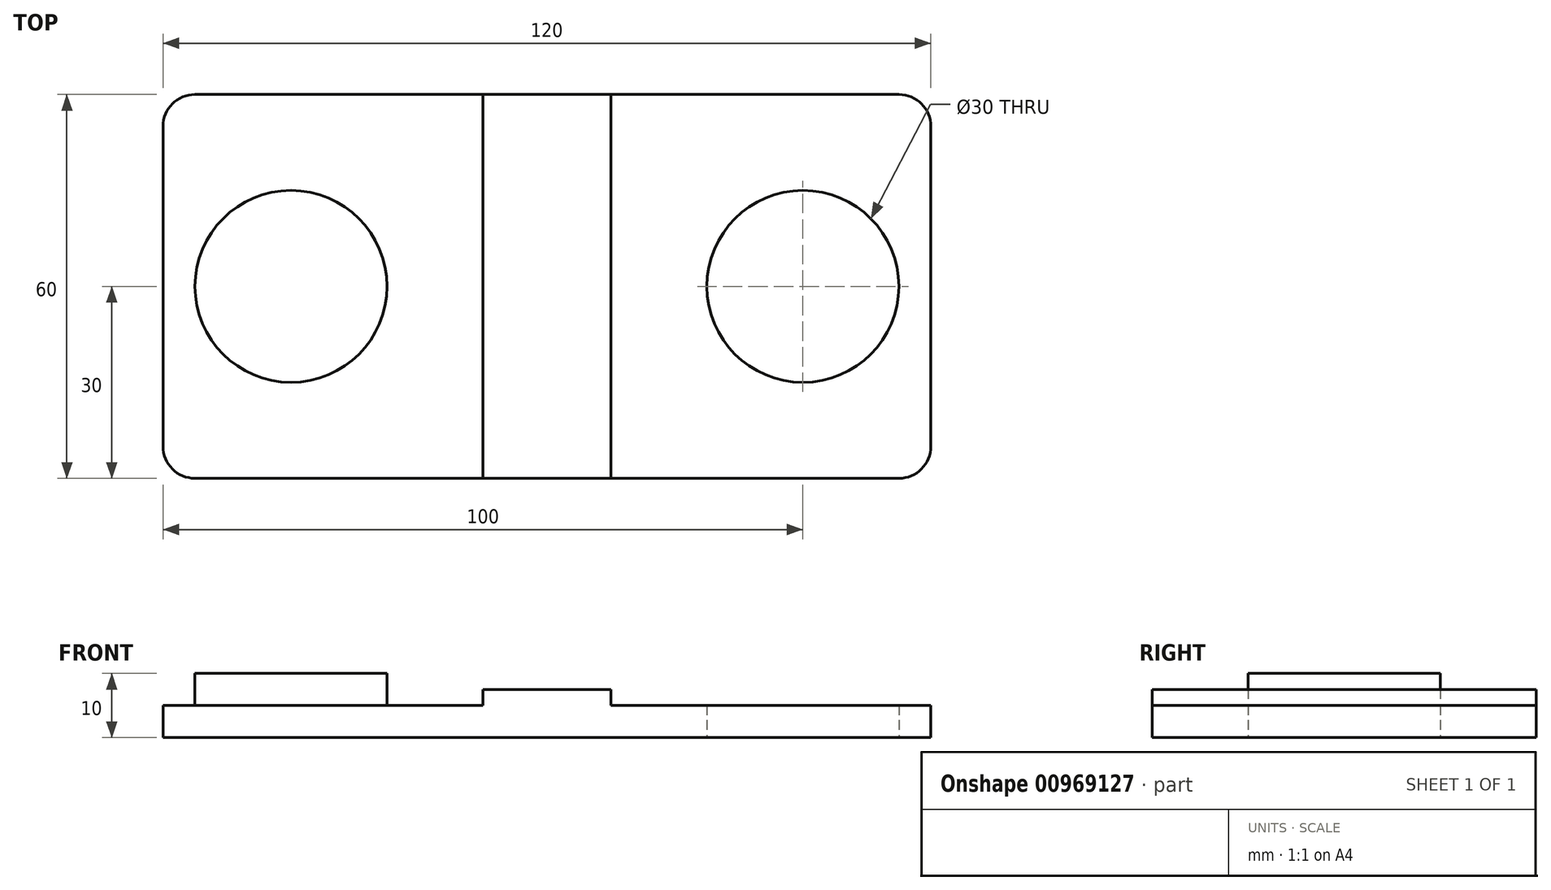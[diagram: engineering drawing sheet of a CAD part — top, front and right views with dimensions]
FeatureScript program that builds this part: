
annotation { "Feature Type Name" : "Feature", "Feature Type Description" : "" }
export const myFeature = defineFeature(function(context is Context, id is Id, definition is map)
    precondition{}
    {
        {
            var Q0;
            Q0=qCreatedBy(makeId("Top.planeOp"),FACE);
            var sketch = newSketch(context, id + "F0", { "sketchPlane" : qUnion([Q0])});
            skLineSegment(sketch, "E0.bottom", {"start": v(60, 30) * mm, "end": v(-60, 30) * mm});
            skLineSegment(sketch, "E0.top", {"start": v(60, -30) * mm, "end": v(-60, -30) * mm});
            skLineSegment(sketch, "E0.left", {"start": v(60, 30) * mm, "end": v(60, -30) * mm});
            skLineSegment(sketch, "E0.right", {"start": v(-60, 30) * mm, "end": v(-60, -30) * mm});
            skPoint(sketch, "E0.middle", {"position": v(0, 0) * mm});
            skCircle(sketch, "E1", {"center": v(40, 0) * mm, "radius": 15 * mm});
            skSolve(sketch);
        }
        {
            var Q0;
            Q0=makeQuery(id+"F0.imprint","IMPRINT",FACE,{"disambiguationData":[TD([[makeQuery(id+"F0.imprint","IMPRINT",EDGE,{"derivedFrom":sQuery(id+"F0.wireOp",EDGE,"E0.bottom")}),1.0]])]});
            extrude(context, id + "F1", {"entities" : qUnion([Q0]), "depth" : 5 * mm, "offsetDistance" : 25 * mm});
        }
        {
            var Q0;
            Q0=makeQuery(id+"F1.opExtrude","SWEPT_EDGE",EDGE,{"disambiguationData":[OSD([sQuery(id+"F0.wireOp",EDGE,"E0.bottom"),sQuery(id+"F0.wireOp",EDGE,"E0.left")])]});
            var Q1;
            Q1=makeQuery(id+"F1.opExtrude","SWEPT_EDGE",EDGE,{"disambiguationData":[OSD([sQuery(id+"F0.wireOp",EDGE,"E0.top"),sQuery(id+"F0.wireOp",EDGE,"E0.left")])]});
            var Q2;
            Q2=makeQuery(id+"F1.opExtrude","SWEPT_EDGE",EDGE,{"disambiguationData":[OSD([sQuery(id+"F0.wireOp",EDGE,"E0.top"),sQuery(id+"F0.wireOp",EDGE,"E0.right")])]});
            var Q3;
            Q3=makeQuery(id+"F1.opExtrude","SWEPT_EDGE",EDGE,{"disambiguationData":[OSD([sQuery(id+"F0.wireOp",EDGE,"E0.bottom"),sQuery(id+"F0.wireOp",EDGE,"E0.right")])]});
            fillet(context, id + "F2", {"entities" : qUnion([Q0, Q1, Q2, Q3]), "radius" : 5 * mm, "tangentPropagation" : true, "allowEdgeOverflow" : false});
        }
        {
            var Q0;
            Q0=makeQuery(id+"F1.opExtrude","CAP_FACE",FACE,{"disambiguationData":[OSD([sQuery(id+"F0.wireOp",EDGE,"E0.bottom"),sQuery(id+"F0.wireOp",EDGE,"E0.top"),sQuery(id+"F0.wireOp",EDGE,"E0.left"),sQuery(id+"F0.wireOp",EDGE,"E0.right"),sQuery(id+"F0.wireOp",EDGE,"E1")])],"isStart":false});
            var sketch = newSketch(context, id + "F3", { "sketchPlane" : qUnion([Q0])});
            skCircle(sketch, "E2", {"center": v(-40, 0) * mm, "radius": 15 * mm});
            skSolve(sketch);
        }
        {
            var Q0;
            Q0=makeQuery(id+"F3.imprint","IMPRINT",FACE,{"disambiguationData":[TD([[makeQuery(id+"F3.imprint","IMPRINT",EDGE,{"derivedFrom":sQuery(id+"F3.wireOp",EDGE,"E2")}),1.0]])]});
            extrude(context, id + "F4", {"entities" : qUnion([Q0]), "operationType" : NewBodyOperationType.ADD, "depth" : 5 * mm, "offsetDistance" : 25 * mm});
        }
        {
            var Q0;
            Q0=makeQuery(id+"F1.opExtrude","CAP_FACE",FACE,{"disambiguationData":[OSD([sQuery(id+"F0.wireOp",EDGE,"E0.bottom"),sQuery(id+"F0.wireOp",EDGE,"E0.top"),sQuery(id+"F0.wireOp",EDGE,"E0.left"),sQuery(id+"F0.wireOp",EDGE,"E0.right"),sQuery(id+"F0.wireOp",EDGE,"E1")])],"isStart":false});
            var sketch = newSketch(context, id + "F5", { "sketchPlane" : qUnion([Q0])});
            skLineSegment(sketch, "E3", {"start": v(-10, 30) * mm, "end": v(-10, -30) * mm});
            skLineSegment(sketch, "E4", {"start": v(-10, -30) * mm, "end": v(10, -30) * mm});
            skLineSegment(sketch, "E5", {"start": v(10, -30) * mm, "end": v(10, 30) * mm});
            skLineSegment(sketch, "E6", {"start": v(10, 30) * mm, "end": v(-10, 30) * mm});
            skSolve(sketch);
        }
        {
            var Q0;
            Q0=makeQuery(id+"F5.imprint","IMPRINT",FACE,{"disambiguationData":[TD([[makeQuery(id+"F5.imprint","IMPRINT",EDGE,{"derivedFrom":sQuery(id+"F5.wireOp",EDGE,"E3")}),1.0]])]});
            extrude(context, id + "F6", {"entities" : qUnion([Q0]), "operationType" : NewBodyOperationType.ADD, "depth" : 2.5 * mm, "offsetDistance" : 25 * mm});
        }
    });
